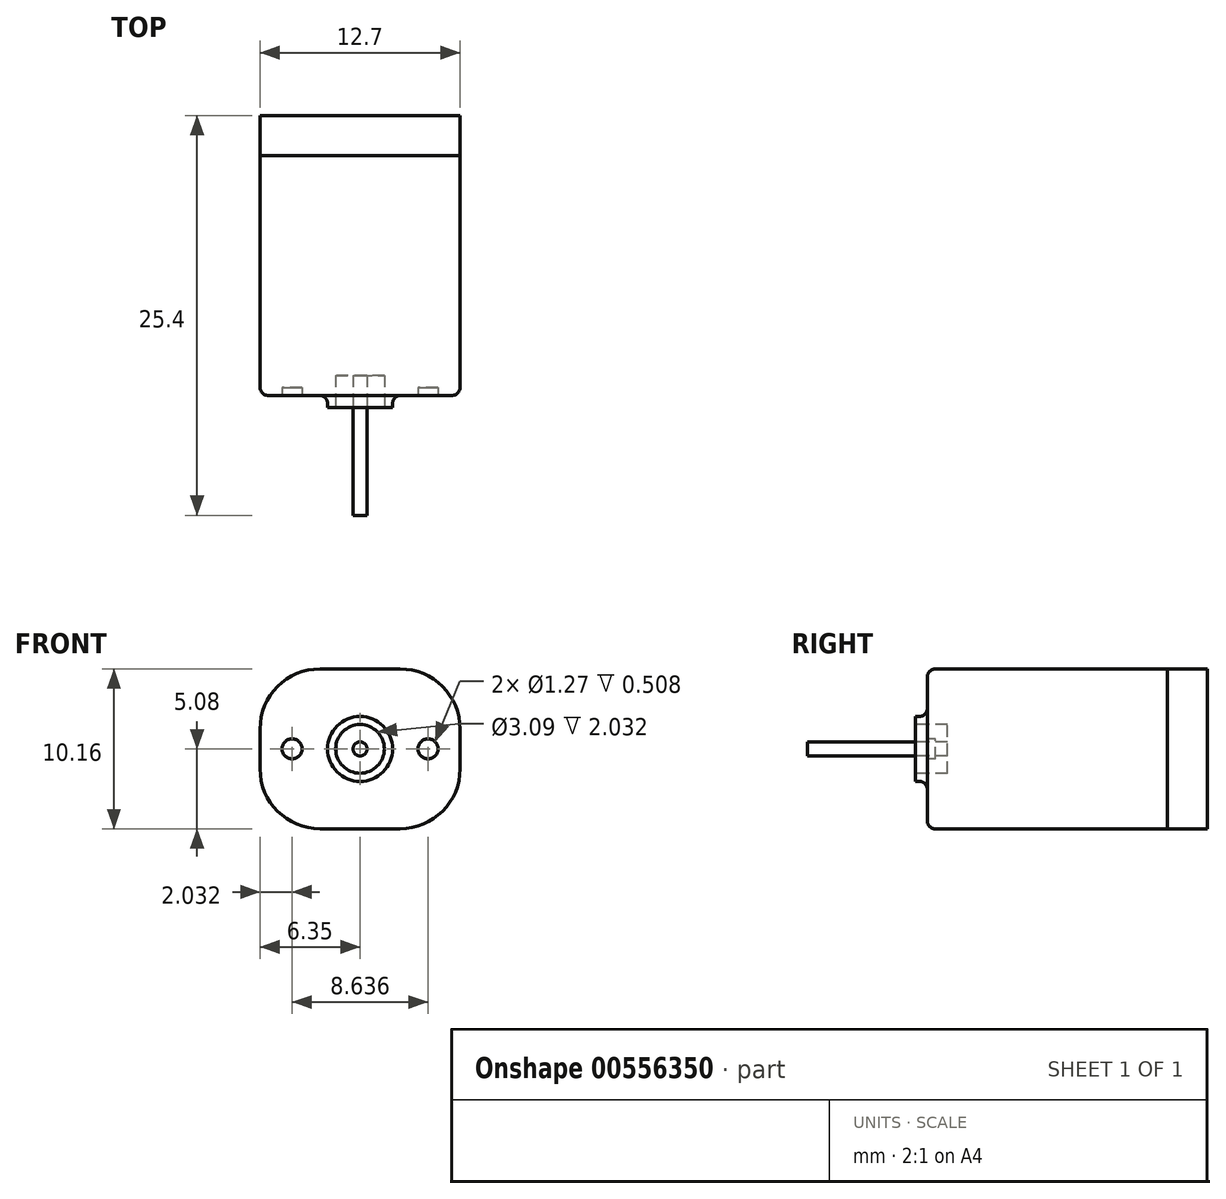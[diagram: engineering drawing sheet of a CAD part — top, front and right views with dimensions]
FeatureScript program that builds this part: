
annotation { "Feature Type Name" : "Feature", "Feature Type Description" : "" }
export const myFeature = defineFeature(function(context is Context, id is Id, definition is map)
    precondition{}
    {
        {
            var Q0;
            Q0=qCreatedBy(makeId("Front.planeOp"),FACE);
            var sketch = newSketch(context, id + "F0", { "sketchPlane" : qUnion([Q0])});
            skLineSegment(sketch, "E0", {"start": v(0, 0) * mm, "end": v(12.7, 0) * mm});
            skLineSegment(sketch, "E1", {"start": v(0, 0) * mm, "end": v(0, 10.16) * mm});
            skLineSegment(sketch, "E2", {"start": v(0, 10.16) * mm, "end": v(12.7, 10.16) * mm});
            skLineSegment(sketch, "E3", {"start": v(12.7, 10.16) * mm, "end": v(12.7, 0) * mm});
            skSolve(sketch);
        }
        {
            var Q0;
            Q0=makeQuery(id+"F0.imprint","IMPRINT",FACE,{"disambiguationData":[TD([[makeQuery(id+"F0.imprint","IMPRINT",EDGE,{"derivedFrom":sQuery(id+"F0.wireOp",EDGE,"E0")}),1.0]])]});
            extrude(context, id + "F1", {"entities" : qUnion([Q0]), "depth" : 15.24 * mm, "offsetDistance" : 25.4 * mm});
        }
        {
            var Q0;
            Q0=makeQuery(id+"F1.opExtrude","SWEPT_EDGE",EDGE,{"disambiguationData":[OSD([sQuery(id+"F0.wireOp",EDGE,"E1"),sQuery(id+"F0.wireOp",EDGE,"E2")])]});
            var Q1;
            Q1=makeQuery(id+"F1.opExtrude","SWEPT_EDGE",EDGE,{"disambiguationData":[OSD([sQuery(id+"F0.wireOp",EDGE,"E2"),sQuery(id+"F0.wireOp",EDGE,"E3")])]});
            var Q2;
            Q2=makeQuery(id+"F1.opExtrude","SWEPT_EDGE",EDGE,{"disambiguationData":[OSD([sQuery(id+"F0.wireOp",EDGE,"E0"),sQuery(id+"F0.wireOp",EDGE,"E1")])]});
            var Q3;
            Q3=makeQuery(id+"F1.opExtrude","SWEPT_EDGE",EDGE,{"disambiguationData":[OSD([sQuery(id+"F0.wireOp",EDGE,"E0"),sQuery(id+"F0.wireOp",EDGE,"E3")])]});
            fillet(context, id + "F2", {"entities" : qUnion([Q0, Q1, Q2, Q3]), "radius" : 3.8 * mm, "tangentPropagation" : true, "allowEdgeOverflow" : false});
        }
        {
            var Q0;
            Q0=makeQuery(id+"F1.opExtrude","CAP_FACE",FACE,{"disambiguationData":[OSD([sQuery(id+"F0.wireOp",EDGE,"E0"),sQuery(id+"F0.wireOp",EDGE,"E1"),sQuery(id+"F0.wireOp",EDGE,"E2"),sQuery(id+"F0.wireOp",EDGE,"E3")])],"isStart":false});
            var sketch = newSketch(context, id + "F3", { "sketchPlane" : qUnion([Q0])});
            skCircle(sketch, "E4", {"center": v(6.35, 5.08) * mm, "radius": 2.06 * mm});
            skCircle(sketch, "E5", {"center": v(6.35, 5.08) * mm, "radius": 1.55 * mm});
            skCircle(sketch, "E6", {"center": v(6.35, 5.08) * mm, "radius": 0.45 * mm});
            skCircle(sketch, "E7", {"center": v(2.03, 5.08) * mm, "radius": 0.64 * mm});
            skCircle(sketch, "E8", {"center": v(10.67, 5.08) * mm, "radius": 0.64 * mm});
            skSolve(sketch);
        }
        {
            var Q0;
            Q0=makeQuery(id+"F3.imprint","IMPRINT",FACE,{"disambiguationData":[TD([[makeQuery(id+"F3.imprint","IMPRINT",EDGE,{"derivedFrom":sQuery(id+"F3.wireOp",EDGE,"E5")}),1.0]])]});
            extrude(context, id + "F4", {"entities" : qUnion([Q0]), "operationType" : NewBodyOperationType.REMOVE, "oppositeDirection" : true, "depth" : 1.27 * mm, "offsetDistance" : 25.4 * mm});
        }
        {
            var Q0;
            Q0=makeQuery(id+"F3.imprint","IMPRINT",FACE,{"disambiguationData":[TD([[makeQuery(id+"F3.imprint","IMPRINT",EDGE,{"derivedFrom":sQuery(id+"F3.wireOp",EDGE,"E4")}),1.0]])]});
            extrude(context, id + "F5", {"entities" : qUnion([Q0]), "operationType" : NewBodyOperationType.ADD, "depth" : 0.76 * mm, "offsetDistance" : 25.4 * mm});
        }
        {
            var Q0;
            Q0=makeQuery(id+"F4.boolean.opBoolean","SPLIT",FACE,{"disambiguationData":[TD([makeQuery(id+"F4.opExtrude","SWEPT_FACE",FACE,{"disambiguationData":[OSD([sQuery(id+"F3.wireOp",EDGE,"E6")])]})])],"derivedFrom":makeQuery(id+"F1.opExtrude","CAP_FACE",FACE,{"disambiguationData":[OSD([sQuery(id+"F0.wireOp",EDGE,"E0"),sQuery(id+"F0.wireOp",EDGE,"E1"),sQuery(id+"F0.wireOp",EDGE,"E2"),sQuery(id+"F0.wireOp",EDGE,"E3")])],"isStart":false})});
            extrude(context, id + "F6", {"entities" : qUnion([Q0]), "operationType" : NewBodyOperationType.ADD, "depth" : 7.62 * mm, "offsetDistance" : 25.4 * mm});
        }
        {
            var Q0;
            {var subQ0=sQuery(id+"F0.wireOp",EDGE,"E2");var subQ1=sQuery(id+"F0.wireOp",EDGE,"E1");var subQ2=sQuery(id+"F0.wireOp",EDGE,"E0");var subQ3=sQuery(id+"F0.wireOp",EDGE,"E3");Q0=makeQuery(id+"F4.boolean.opBoolean","SPLIT",FACE,{"disambiguationData":[TD([makeQuery(id+"F1.opExtrude","SWEPT_FACE",FACE,{"disambiguationData":[OSD([subQ2])]})])],"derivedFrom":makeQuery(id+"F1.opExtrude","CAP_FACE",FACE,{"disambiguationData":[OSD([subQ2,subQ1,subQ0,subQ3])],"isStart":false})});}
            fillet(context, id + "F7", {"entities" : qUnion([Q0]), "radius" : 0.5 * mm, "tangentPropagation" : true, "allowEdgeOverflow" : false});
        }
        {
            var Q0;
            Q0=makeQuery(id+"F3.imprint","IMPRINT",FACE,{"disambiguationData":[TD([[makeQuery(id+"F3.imprint","IMPRINT",EDGE,{"derivedFrom":sQuery(id+"F3.wireOp",EDGE,"E7")}),1.0]])]});
            var Q1;
            Q1=makeQuery(id+"F3.imprint","IMPRINT",FACE,{"disambiguationData":[TD([[makeQuery(id+"F3.imprint","IMPRINT",EDGE,{"derivedFrom":sQuery(id+"F3.wireOp",EDGE,"E8")}),1.0]])]});
            extrude(context, id + "F8", {"entities" : qUnion([Q0, Q1]), "operationType" : NewBodyOperationType.REMOVE, "oppositeDirection" : true, "depth" : 0.5 * mm, "offsetDistance" : 25.4 * mm});
        }
        {
            var Q0;
            Q0=makeQuery(id+"F1.opExtrude","CAP_FACE",FACE,{"disambiguationData":[OSD([sQuery(id+"F0.wireOp",EDGE,"E0"),sQuery(id+"F0.wireOp",EDGE,"E1"),sQuery(id+"F0.wireOp",EDGE,"E2"),sQuery(id+"F0.wireOp",EDGE,"E3")])],"isStart":true});
            extrude(context, id + "F9", {"entities" : qUnion([Q0]), "depth" : 2.54 * mm, "offsetDistance" : 25.4 * mm});
        }
    });
